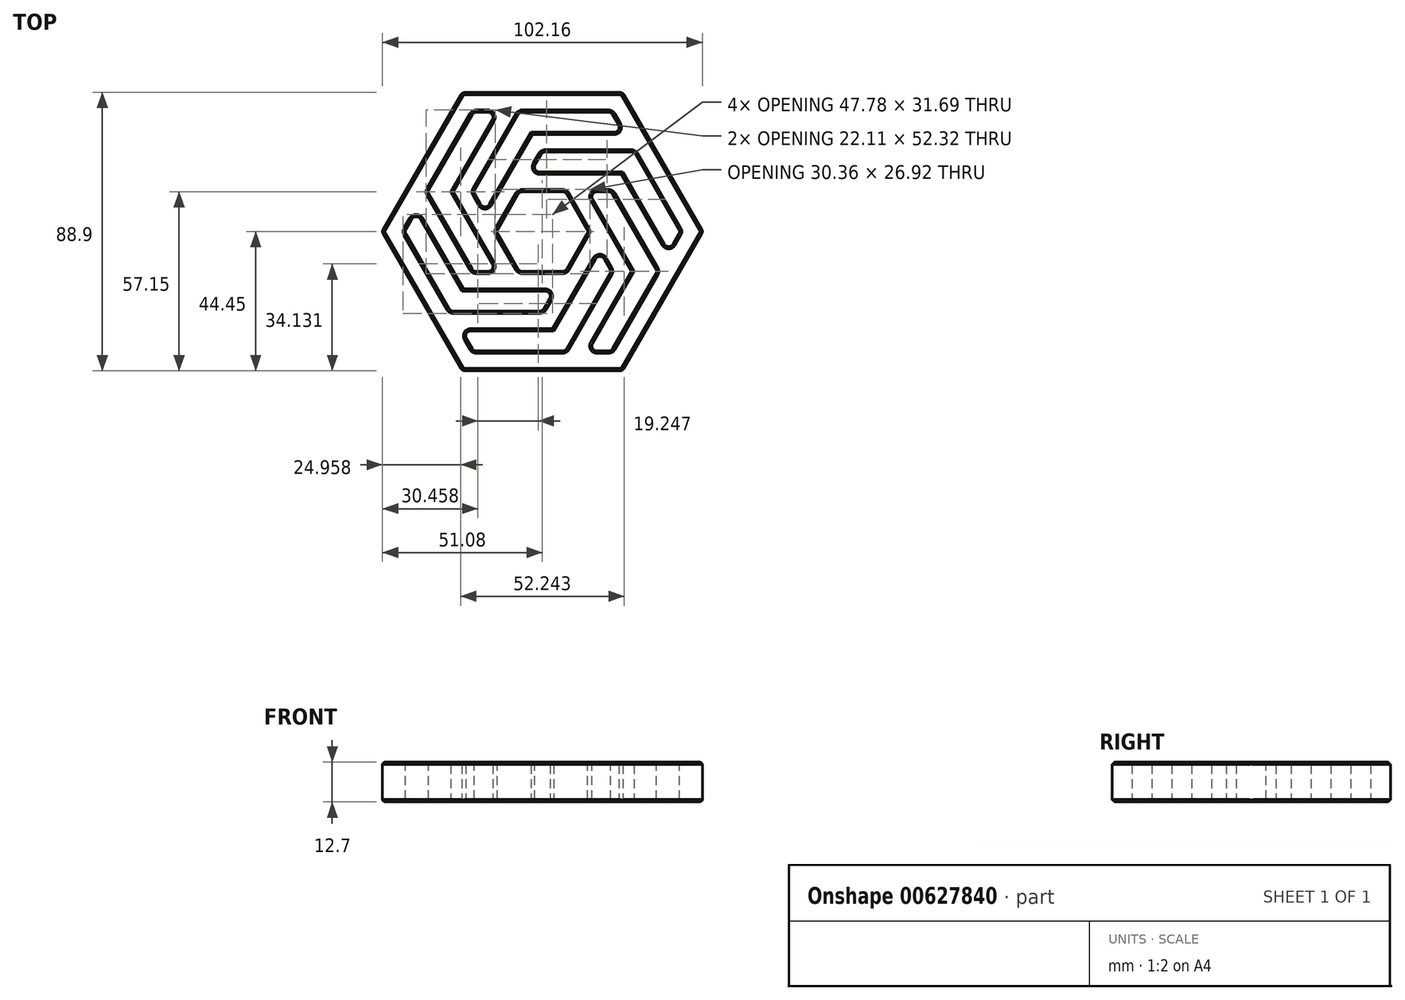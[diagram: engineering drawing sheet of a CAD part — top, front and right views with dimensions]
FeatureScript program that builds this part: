
annotation { "Feature Type Name" : "Feature", "Feature Type Description" : "" }
export const myFeature = defineFeature(function(context is Context, id is Id, definition is map)
    precondition{}
    {
        {
            var Q0;
            Q0=qCreatedBy(makeId("Top.planeOp"),FACE);
            var sketch = newSketch(context, id + "F0", { "sketchPlane" : qUnion([Q0])});
            skCircle(sketch, "E0.cCircle", {"center": v(0, 0) * mm, "radius": 44.45 * mm, "construction": true});
            skLineSegment(sketch, "E0.0", {"start": v(-25.66, 44.45) * mm, "end": v(25.66, 44.45) * mm});
            skLineSegment(sketch, "E0.1", {"start": v(25.66, 44.45) * mm, "end": v(51.33, 0) * mm});
            skLineSegment(sketch, "E0.2", {"start": v(51.33, 0) * mm, "end": v(25.66, -44.45) * mm});
            skLineSegment(sketch, "E0.3", {"start": v(25.66, -44.45) * mm, "end": v(-25.66, -44.45) * mm});
            skLineSegment(sketch, "E0.4", {"start": v(-25.66, -44.45) * mm, "end": v(-51.33, 0) * mm});
            skLineSegment(sketch, "E0.5", {"start": v(-51.33, 0) * mm, "end": v(-25.66, 44.45) * mm});
            skPoint(sketch, "E0.0.midPoint", {"position": v(0, 44.45) * mm});
            skCircle(sketch, "E1.cCircle", {"center": v(0, 0) * mm, "radius": 12.7 * mm, "construction": true});
            skLineSegment(sketch, "E1.0", {"start": v(-7.33, 12.7) * mm, "end": v(7.33, 12.7) * mm});
            skLineSegment(sketch, "E1.1", {"start": v(7.33, 12.7) * mm, "end": v(14.66, 0) * mm});
            skLineSegment(sketch, "E1.2", {"start": v(14.66, 0) * mm, "end": v(7.33, -12.7) * mm});
            skLineSegment(sketch, "E1.3", {"start": v(7.33, -12.7) * mm, "end": v(-7.33, -12.7) * mm});
            skLineSegment(sketch, "E1.4", {"start": v(-7.33, -12.7) * mm, "end": v(-14.66, 0) * mm});
            skLineSegment(sketch, "E1.5", {"start": v(-14.66, 0) * mm, "end": v(-7.33, 12.7) * mm});
            skPoint(sketch, "E1.0.midPoint", {"position": v(0, 12.7) * mm});
            skLineSegment(sketch, "E2", {"start": v(3.67, -19.05) * mm, "end": v(-25.66, -19.05) * mm});
            skLineSegment(sketch, "E3", {"start": v(-14.66, -12.7) * mm, "end": v(-29.33, 12.7) * mm});
            skLineSegment(sketch, "E4", {"start": v(25.66, 19.05) * mm, "end": v(-3.67, 19.05) * mm});
            skLineSegment(sketch, "E5", {"start": v(29.33, -12.7) * mm, "end": v(14.66, 12.7) * mm});
            skLineSegment(sketch, "E6", {"start": v(18.33, -6.35) * mm, "end": v(3.67, -31.75) * mm});
            skLineSegment(sketch, "E7", {"start": v(3.67, -19.05) * mm, "end": v(0, -25.4) * mm});
            skLineSegment(sketch, "E8", {"start": v(-14.66, -12.7) * mm, "end": v(-22, -12.7) * mm});
            skLineSegment(sketch, "E9", {"start": v(-18.33, 6.35) * mm, "end": v(-22, 12.7) * mm});
            skLineSegment(sketch, "E10", {"start": v(-3.67, 19.05) * mm, "end": v(0, 25.4) * mm});
            skLineSegment(sketch, "E11", {"start": v(14.66, 12.7) * mm, "end": v(22, 12.7) * mm});
            skLineSegment(sketch, "E12", {"start": v(18.33, -6.35) * mm, "end": v(22, -12.7) * mm});
            skCircle(sketch, "E13.cCircle", {"center": v(0, 0) * mm, "radius": 38.1 * mm, "construction": true});
            skLineSegment(sketch, "E13.0", {"start": v(-22, 38.1) * mm, "end": v(-14.66, 38.1) * mm});
            skLineSegment(sketch, "E13.1", {"start": v(29.33, 25.4) * mm, "end": v(44, 0) * mm});
            skLineSegment(sketch, "E13.2", {"start": v(44, 0) * mm, "end": v(40.33, -6.35) * mm});
            skLineSegment(sketch, "E13.3", {"start": v(22, -38.1) * mm, "end": v(14.66, -38.1) * mm});
            skLineSegment(sketch, "E13.4", {"start": v(-22, -38.1) * mm, "end": v(-25.66, -31.75) * mm});
            skLineSegment(sketch, "E13.5", {"start": v(-44, 0) * mm, "end": v(-40.33, 6.35) * mm});
            skPoint(sketch, "E13.0.midPoint", {"position": v(0, 38.1) * mm});
            skLineSegment(sketch, "E14", {"start": v(-22, -12.7) * mm, "end": v(-36.66, 12.7) * mm});
            skLineSegment(sketch, "E15", {"start": v(-40.33, 6.35) * mm, "end": v(-25.66, -19.05) * mm});
            skLineSegment(sketch, "E16", {"start": v(-22, 12.7) * mm, "end": v(-7.33, 38.1) * mm});
            skLineSegment(sketch, "E17", {"start": v(0, 25.4) * mm, "end": v(29.33, 25.4) * mm});
            skLineSegment(sketch, "E18", {"start": v(-29.33, 12.7) * mm, "end": v(-14.66, 38.1) * mm});
            skLineSegment(sketch, "E19", {"start": v(-3.67, 31.75) * mm, "end": v(25.66, 31.75) * mm});
            skLineSegment(sketch, "E20.trimOffspring", {"start": v(6.96, 37.46) * mm, "end": v(7.33, 38.1) * mm});
            skLineSegment(sketch, "E21", {"start": v(-18.33, 6.35) * mm, "end": v(-3.67, 31.75) * mm});
            skLineSegment(sketch, "E22", {"start": v(22, 12.7) * mm, "end": v(36.66, -12.7) * mm});
            skLineSegment(sketch, "E23", {"start": v(25.66, 19.05) * mm, "end": v(40.33, -6.35) * mm});
            skLineSegment(sketch, "E24", {"start": v(22, -12.7) * mm, "end": v(7.33, -38.1) * mm});
            skLineSegment(sketch, "E25", {"start": v(29.33, -12.7) * mm, "end": v(14.66, -38.1) * mm});
            skLineSegment(sketch, "E26", {"start": v(3.67, -31.75) * mm, "end": v(-25.66, -31.75) * mm});
            skLineSegment(sketch, "E27", {"start": v(0, -25.4) * mm, "end": v(-29.33, -25.4) * mm});
            skLineSegment(sketch, "E28.trimOffspring", {"start": v(7.33, -38.1) * mm, "end": v(-22, -38.1) * mm});
            skLineSegment(sketch, "E29.trimOffspring", {"start": v(-29.33, -25.4) * mm, "end": v(-44, 0) * mm});
            skLineSegment(sketch, "E30.trimOffspring", {"start": v(-36.66, 12.7) * mm, "end": v(-22, 38.1) * mm});
            skLineSegment(sketch, "E31.trimOffspring", {"start": v(-7.33, 38.1) * mm, "end": v(22, 38.1) * mm});
            skLineSegment(sketch, "E32.trimOffspring", {"start": v(36.66, -12.7) * mm, "end": v(22, -38.1) * mm});
            skLineSegment(sketch, "E33", {"start": v(22, 38.1) * mm, "end": v(25.66, 31.75) * mm});
            skSolve(sketch);
        }
        {
            var Q0;
            Q0=makeQuery(id+"F0.imprint","IMPRINT",FACE,{"disambiguationData":[TD([[makeQuery(id+"F0.imprint","IMPRINT",EDGE,{"derivedFrom":sQuery(id+"F0.wireOp",EDGE,"E0.0")}),-1.0]])]});
            extrude(context, id + "F1", {"entities" : qUnion([Q0]), "depth" : 12.7 * mm, "offsetDistance" : 25.4 * mm});
        }
        {
            var Q0;
            Q0=makeQuery(id+"F1.opExtrude","SWEPT_EDGE",EDGE,{"disambiguationData":[OSD([sQuery(id+"F0.wireOp",EDGE,"E1.1"),sQuery(id+"F0.wireOp",EDGE,"E1.2")])]});
            var Q1;
            Q1=makeQuery(id+"F1.opExtrude","SWEPT_EDGE",EDGE,{"disambiguationData":[OSD([sQuery(id+"F0.wireOp",EDGE,"E1.2"),sQuery(id+"F0.wireOp",EDGE,"E1.3")])]});
            var Q2;
            Q2=makeQuery(id+"F1.opExtrude","SWEPT_EDGE",EDGE,{"disambiguationData":[OSD([sQuery(id+"F0.wireOp",EDGE,"E1.3"),sQuery(id+"F0.wireOp",EDGE,"E1.4")])]});
            var Q3;
            Q3=makeQuery(id+"F1.opExtrude","SWEPT_EDGE",EDGE,{"disambiguationData":[OSD([sQuery(id+"F0.wireOp",EDGE,"E1.4"),sQuery(id+"F0.wireOp",EDGE,"E1.5")])]});
            var Q4;
            Q4=makeQuery(id+"F1.opExtrude","SWEPT_EDGE",EDGE,{"disambiguationData":[OSD([sQuery(id+"F0.wireOp",EDGE,"E1.0"),sQuery(id+"F0.wireOp",EDGE,"E1.5")])]});
            var Q5;
            Q5=makeQuery(id+"F1.opExtrude","SWEPT_EDGE",EDGE,{"disambiguationData":[OSD([sQuery(id+"F0.wireOp",EDGE,"E1.0"),sQuery(id+"F0.wireOp",EDGE,"E1.1")])]});
            var Q6;
            Q6=makeQuery(id+"F1.opExtrude","SWEPT_EDGE",EDGE,{"disambiguationData":[OSD([sQuery(id+"F0.wireOp",EDGE,"E13.3"),sQuery(id+"F0.wireOp",EDGE,"E25")])]});
            var Q7;
            Q7=makeQuery(id+"F1.opExtrude","SWEPT_EDGE",EDGE,{"disambiguationData":[OSD([sQuery(id+"F0.wireOp",EDGE,"E13.3"),sQuery(id+"F0.wireOp",EDGE,"E32.trimOffspring")])]});
            var Q8;
            Q8=makeQuery(id+"F1.opExtrude","SWEPT_EDGE",EDGE,{"disambiguationData":[OSD([sQuery(id+"F0.wireOp",EDGE,"E22"),sQuery(id+"F0.wireOp",EDGE,"E32.trimOffspring")])]});
            var Q9;
            Q9=makeQuery(id+"F1.opExtrude","SWEPT_EDGE",EDGE,{"disambiguationData":[OSD([sQuery(id+"F0.wireOp",EDGE,"E11"),sQuery(id+"F0.wireOp",EDGE,"E22")])]});
            var Q10;
            Q10=makeQuery(id+"F1.opExtrude","SWEPT_EDGE",EDGE,{"disambiguationData":[OSD([sQuery(id+"F0.wireOp",EDGE,"E5"),sQuery(id+"F0.wireOp",EDGE,"E11")])]});
            var Q11;
            Q11=makeQuery(id+"F1.opExtrude","SWEPT_EDGE",EDGE,{"disambiguationData":[OSD([sQuery(id+"F0.wireOp",EDGE,"E13.2"),sQuery(id+"F0.wireOp",EDGE,"E23")])]});
            var Q12;
            Q12=makeQuery(id+"F1.opExtrude","SWEPT_EDGE",EDGE,{"disambiguationData":[OSD([sQuery(id+"F0.wireOp",EDGE,"E13.1"),sQuery(id+"F0.wireOp",EDGE,"E13.2")])]});
            var Q13;
            Q13=makeQuery(id+"F1.opExtrude","SWEPT_EDGE",EDGE,{"disambiguationData":[OSD([sQuery(id+"F0.wireOp",EDGE,"E13.1"),sQuery(id+"F0.wireOp",EDGE,"E17")])]});
            var Q14;
            Q14=makeQuery(id+"F1.opExtrude","SWEPT_EDGE",EDGE,{"disambiguationData":[OSD([sQuery(id+"F0.wireOp",EDGE,"E10"),sQuery(id+"F0.wireOp",EDGE,"E17")])]});
            var Q15;
            Q15=makeQuery(id+"F1.opExtrude","SWEPT_EDGE",EDGE,{"disambiguationData":[OSD([sQuery(id+"F0.wireOp",EDGE,"E4"),sQuery(id+"F0.wireOp",EDGE,"E10")])]});
            var Q16;
            Q16=makeQuery(id+"F1.opExtrude","SWEPT_EDGE",EDGE,{"disambiguationData":[OSD([sQuery(id+"F0.wireOp",EDGE,"E31.trimOffspring"),sQuery(id+"F0.wireOp",EDGE,"E33")])]});
            var Q17;
            Q17=makeQuery(id+"F1.opExtrude","SWEPT_EDGE",EDGE,{"disambiguationData":[OSD([sQuery(id+"F0.wireOp",EDGE,"E19"),sQuery(id+"F0.wireOp",EDGE,"E33")])]});
            var Q18;
            Q18=makeQuery(id+"F1.opExtrude","SWEPT_EDGE",EDGE,{"disambiguationData":[OSD([sQuery(id+"F0.wireOp",EDGE,"E16"),sQuery(id+"F0.wireOp",EDGE,"E31.trimOffspring")])]});
            var Q19;
            Q19=makeQuery(id+"F1.opExtrude","SWEPT_EDGE",EDGE,{"disambiguationData":[OSD([sQuery(id+"F0.wireOp",EDGE,"E9"),sQuery(id+"F0.wireOp",EDGE,"E16")])]});
            var Q20;
            Q20=makeQuery(id+"F1.opExtrude","SWEPT_EDGE",EDGE,{"disambiguationData":[OSD([sQuery(id+"F0.wireOp",EDGE,"E9"),sQuery(id+"F0.wireOp",EDGE,"E21")])]});
            var Q21;
            Q21=makeQuery(id+"F1.opExtrude","SWEPT_EDGE",EDGE,{"disambiguationData":[OSD([sQuery(id+"F0.wireOp",EDGE,"E13.0"),sQuery(id+"F0.wireOp",EDGE,"E18")])]});
            var Q22;
            Q22=makeQuery(id+"F1.opExtrude","SWEPT_EDGE",EDGE,{"disambiguationData":[OSD([sQuery(id+"F0.wireOp",EDGE,"E13.0"),sQuery(id+"F0.wireOp",EDGE,"E30.trimOffspring")])]});
            var Q23;
            Q23=makeQuery(id+"F1.opExtrude","SWEPT_EDGE",EDGE,{"disambiguationData":[OSD([sQuery(id+"F0.wireOp",EDGE,"E14"),sQuery(id+"F0.wireOp",EDGE,"E30.trimOffspring")])]});
            var Q24;
            Q24=makeQuery(id+"F1.opExtrude","SWEPT_EDGE",EDGE,{"disambiguationData":[OSD([sQuery(id+"F0.wireOp",EDGE,"E8"),sQuery(id+"F0.wireOp",EDGE,"E14")])]});
            var Q25;
            Q25=makeQuery(id+"F1.opExtrude","SWEPT_EDGE",EDGE,{"disambiguationData":[OSD([sQuery(id+"F0.wireOp",EDGE,"E3"),sQuery(id+"F0.wireOp",EDGE,"E8")])]});
            var Q26;
            Q26=makeQuery(id+"F1.opExtrude","SWEPT_EDGE",EDGE,{"disambiguationData":[OSD([sQuery(id+"F0.wireOp",EDGE,"E13.5"),sQuery(id+"F0.wireOp",EDGE,"E15")])]});
            var Q27;
            Q27=makeQuery(id+"F1.opExtrude","SWEPT_EDGE",EDGE,{"disambiguationData":[OSD([sQuery(id+"F0.wireOp",EDGE,"E13.5"),sQuery(id+"F0.wireOp",EDGE,"E29.trimOffspring")])]});
            var Q28;
            Q28=makeQuery(id+"F1.opExtrude","SWEPT_EDGE",EDGE,{"disambiguationData":[OSD([sQuery(id+"F0.wireOp",EDGE,"E27"),sQuery(id+"F0.wireOp",EDGE,"E29.trimOffspring")])]});
            var Q29;
            Q29=makeQuery(id+"F1.opExtrude","SWEPT_EDGE",EDGE,{"disambiguationData":[OSD([sQuery(id+"F0.wireOp",EDGE,"E7"),sQuery(id+"F0.wireOp",EDGE,"E27")])]});
            var Q30;
            Q30=makeQuery(id+"F1.opExtrude","SWEPT_EDGE",EDGE,{"disambiguationData":[OSD([sQuery(id+"F0.wireOp",EDGE,"E2"),sQuery(id+"F0.wireOp",EDGE,"E7")])]});
            var Q31;
            Q31=makeQuery(id+"F1.opExtrude","SWEPT_EDGE",EDGE,{"disambiguationData":[OSD([sQuery(id+"F0.wireOp",EDGE,"E13.4"),sQuery(id+"F0.wireOp",EDGE,"E26")])]});
            var Q32;
            Q32=makeQuery(id+"F1.opExtrude","SWEPT_EDGE",EDGE,{"disambiguationData":[OSD([sQuery(id+"F0.wireOp",EDGE,"E13.4"),sQuery(id+"F0.wireOp",EDGE,"E28.trimOffspring")])]});
            var Q33;
            Q33=makeQuery(id+"F1.opExtrude","SWEPT_EDGE",EDGE,{"disambiguationData":[OSD([sQuery(id+"F0.wireOp",EDGE,"E24"),sQuery(id+"F0.wireOp",EDGE,"E28.trimOffspring")])]});
            var Q34;
            Q34=makeQuery(id+"F1.opExtrude","SWEPT_EDGE",EDGE,{"disambiguationData":[OSD([sQuery(id+"F0.wireOp",EDGE,"E12"),sQuery(id+"F0.wireOp",EDGE,"E24")])]});
            var Q35;
            Q35=makeQuery(id+"F1.opExtrude","SWEPT_EDGE",EDGE,{"disambiguationData":[OSD([sQuery(id+"F0.wireOp",EDGE,"E6"),sQuery(id+"F0.wireOp",EDGE,"E12")])]});
            fillet(context, id + "F2", {"entities" : qUnion([Q0, Q1, Q2, Q3, Q4, Q5, Q6, Q7, Q8, Q9, Q10, Q11, Q12, Q13, Q14, Q15, Q16, Q17, Q18, Q19, Q20, Q21, Q22, Q23, Q24, Q25, Q26, Q27, Q28, Q29, Q30, Q31, Q32, Q33, Q34, Q35]), "radius" : 1.59 * mm, "tangentPropagation" : true, "allowEdgeOverflow" : false});
        }
        {
            var Q0;
            Q0=makeQuery(id+"F1.opExtrude","CAP_FACE",FACE,{"disambiguationData":[OSD([sQuery(id+"F0.wireOp",EDGE,"E0.0"),sQuery(id+"F0.wireOp",EDGE,"E0.1"),sQuery(id+"F0.wireOp",EDGE,"E0.2"),sQuery(id+"F0.wireOp",EDGE,"E0.3"),sQuery(id+"F0.wireOp",EDGE,"E0.4"),sQuery(id+"F0.wireOp",EDGE,"E0.5"),sQuery(id+"F0.wireOp",EDGE,"E1.0"),sQuery(id+"F0.wireOp",EDGE,"E1.1"),sQuery(id+"F0.wireOp",EDGE,"E1.2"),sQuery(id+"F0.wireOp",EDGE,"E1.3"),sQuery(id+"F0.wireOp",EDGE,"E1.4"),sQuery(id+"F0.wireOp",EDGE,"E1.5"),sQuery(id+"F0.wireOp",EDGE,"E2"),sQuery(id+"F0.wireOp",EDGE,"E3"),sQuery(id+"F0.wireOp",EDGE,"E4"),sQuery(id+"F0.wireOp",EDGE,"E5"),sQuery(id+"F0.wireOp",EDGE,"E6"),sQuery(id+"F0.wireOp",EDGE,"E7"),sQuery(id+"F0.wireOp",EDGE,"E8"),sQuery(id+"F0.wireOp",EDGE,"E9"),sQuery(id+"F0.wireOp",EDGE,"E10"),sQuery(id+"F0.wireOp",EDGE,"E11"),sQuery(id+"F0.wireOp",EDGE,"E12"),sQuery(id+"F0.wireOp",EDGE,"E13.0"),sQuery(id+"F0.wireOp",EDGE,"E13.1"),sQuery(id+"F0.wireOp",EDGE,"E13.2"),sQuery(id+"F0.wireOp",EDGE,"E13.3"),sQuery(id+"F0.wireOp",EDGE,"E13.4"),sQuery(id+"F0.wireOp",EDGE,"E13.5"),sQuery(id+"F0.wireOp",EDGE,"E14"),sQuery(id+"F0.wireOp",EDGE,"E15"),sQuery(id+"F0.wireOp",EDGE,"E16"),sQuery(id+"F0.wireOp",EDGE,"E17"),sQuery(id+"F0.wireOp",EDGE,"E18"),sQuery(id+"F0.wireOp",EDGE,"E19"),sQuery(id+"F0.wireOp",EDGE,"E21"),sQuery(id+"F0.wireOp",EDGE,"E22"),sQuery(id+"F0.wireOp",EDGE,"E23"),sQuery(id+"F0.wireOp",EDGE,"E24"),sQuery(id+"F0.wireOp",EDGE,"E25"),sQuery(id+"F0.wireOp",EDGE,"E26"),sQuery(id+"F0.wireOp",EDGE,"E27"),sQuery(id+"F0.wireOp",EDGE,"E28.trimOffspring"),sQuery(id+"F0.wireOp",EDGE,"E29.trimOffspring"),sQuery(id+"F0.wireOp",EDGE,"E30.trimOffspring"),sQuery(id+"F0.wireOp",EDGE,"E31.trimOffspring"),sQuery(id+"F0.wireOp",EDGE,"E32.trimOffspring"),sQuery(id+"F0.wireOp",EDGE,"E33")])],"isStart":false});
            chamfer(context, id + "F3", {"entities" : qUnion([Q0]), "width" : 0.76 * mm, "tangentPropagation" : true});
        }
        {
            var Q0;
            Q0=makeQuery(id+"F1.opExtrude","CAP_FACE",FACE,{"disambiguationData":[OSD([sQuery(id+"F0.wireOp",EDGE,"E0.0"),sQuery(id+"F0.wireOp",EDGE,"E0.1"),sQuery(id+"F0.wireOp",EDGE,"E0.2"),sQuery(id+"F0.wireOp",EDGE,"E0.3"),sQuery(id+"F0.wireOp",EDGE,"E0.4"),sQuery(id+"F0.wireOp",EDGE,"E0.5"),sQuery(id+"F0.wireOp",EDGE,"E1.0"),sQuery(id+"F0.wireOp",EDGE,"E1.1"),sQuery(id+"F0.wireOp",EDGE,"E1.2"),sQuery(id+"F0.wireOp",EDGE,"E1.3"),sQuery(id+"F0.wireOp",EDGE,"E1.4"),sQuery(id+"F0.wireOp",EDGE,"E1.5"),sQuery(id+"F0.wireOp",EDGE,"E2"),sQuery(id+"F0.wireOp",EDGE,"E3"),sQuery(id+"F0.wireOp",EDGE,"E4"),sQuery(id+"F0.wireOp",EDGE,"E5"),sQuery(id+"F0.wireOp",EDGE,"E6"),sQuery(id+"F0.wireOp",EDGE,"E7"),sQuery(id+"F0.wireOp",EDGE,"E8"),sQuery(id+"F0.wireOp",EDGE,"E9"),sQuery(id+"F0.wireOp",EDGE,"E10"),sQuery(id+"F0.wireOp",EDGE,"E11"),sQuery(id+"F0.wireOp",EDGE,"E12"),sQuery(id+"F0.wireOp",EDGE,"E13.0"),sQuery(id+"F0.wireOp",EDGE,"E13.1"),sQuery(id+"F0.wireOp",EDGE,"E13.2"),sQuery(id+"F0.wireOp",EDGE,"E13.3"),sQuery(id+"F0.wireOp",EDGE,"E13.4"),sQuery(id+"F0.wireOp",EDGE,"E13.5"),sQuery(id+"F0.wireOp",EDGE,"E14"),sQuery(id+"F0.wireOp",EDGE,"E15"),sQuery(id+"F0.wireOp",EDGE,"E16"),sQuery(id+"F0.wireOp",EDGE,"E17"),sQuery(id+"F0.wireOp",EDGE,"E18"),sQuery(id+"F0.wireOp",EDGE,"E19"),sQuery(id+"F0.wireOp",EDGE,"E21"),sQuery(id+"F0.wireOp",EDGE,"E22"),sQuery(id+"F0.wireOp",EDGE,"E23"),sQuery(id+"F0.wireOp",EDGE,"E24"),sQuery(id+"F0.wireOp",EDGE,"E25"),sQuery(id+"F0.wireOp",EDGE,"E26"),sQuery(id+"F0.wireOp",EDGE,"E27"),sQuery(id+"F0.wireOp",EDGE,"E28.trimOffspring"),sQuery(id+"F0.wireOp",EDGE,"E29.trimOffspring"),sQuery(id+"F0.wireOp",EDGE,"E30.trimOffspring"),sQuery(id+"F0.wireOp",EDGE,"E31.trimOffspring"),sQuery(id+"F0.wireOp",EDGE,"E32.trimOffspring"),sQuery(id+"F0.wireOp",EDGE,"E33")])],"isStart":true});
            chamfer(context, id + "F4", {"entities" : qUnion([Q0]), "width" : 0.76 * mm, "tangentPropagation" : true});
        }
        {
            var Q0;
            Q0=makeQuery(id+"F1.opExtrude","SWEPT_EDGE",EDGE,{"disambiguationData":[OSD([sQuery(id+"F0.wireOp",EDGE,"E0.4"),sQuery(id+"F0.wireOp",EDGE,"E0.5")])]});
            var Q1;
            Q1=makeQuery(id+"F1.opExtrude","SWEPT_EDGE",EDGE,{"disambiguationData":[OSD([sQuery(id+"F0.wireOp",EDGE,"E0.3"),sQuery(id+"F0.wireOp",EDGE,"E0.4")])]});
            var Q2;
            Q2=makeQuery(id+"F1.opExtrude","SWEPT_EDGE",EDGE,{"disambiguationData":[OSD([sQuery(id+"F0.wireOp",EDGE,"E0.2"),sQuery(id+"F0.wireOp",EDGE,"E0.3")])]});
            var Q3;
            Q3=makeQuery(id+"F1.opExtrude","SWEPT_EDGE",EDGE,{"disambiguationData":[OSD([sQuery(id+"F0.wireOp",EDGE,"E0.1"),sQuery(id+"F0.wireOp",EDGE,"E0.2")])]});
            var Q4;
            Q4=makeQuery(id+"F1.opExtrude","SWEPT_EDGE",EDGE,{"disambiguationData":[OSD([sQuery(id+"F0.wireOp",EDGE,"E0.0"),sQuery(id+"F0.wireOp",EDGE,"E0.1")])]});
            var Q5;
            Q5=makeQuery(id+"F1.opExtrude","SWEPT_EDGE",EDGE,{"disambiguationData":[OSD([sQuery(id+"F0.wireOp",EDGE,"E0.0"),sQuery(id+"F0.wireOp",EDGE,"E0.5")])]});
            fillet(context, id + "F5", {"entities" : qUnion([Q0, Q1, Q2, Q3, Q4, Q5]), "radius" : 1.59 * mm, "tangentPropagation" : true, "allowEdgeOverflow" : false});
        }
    });
